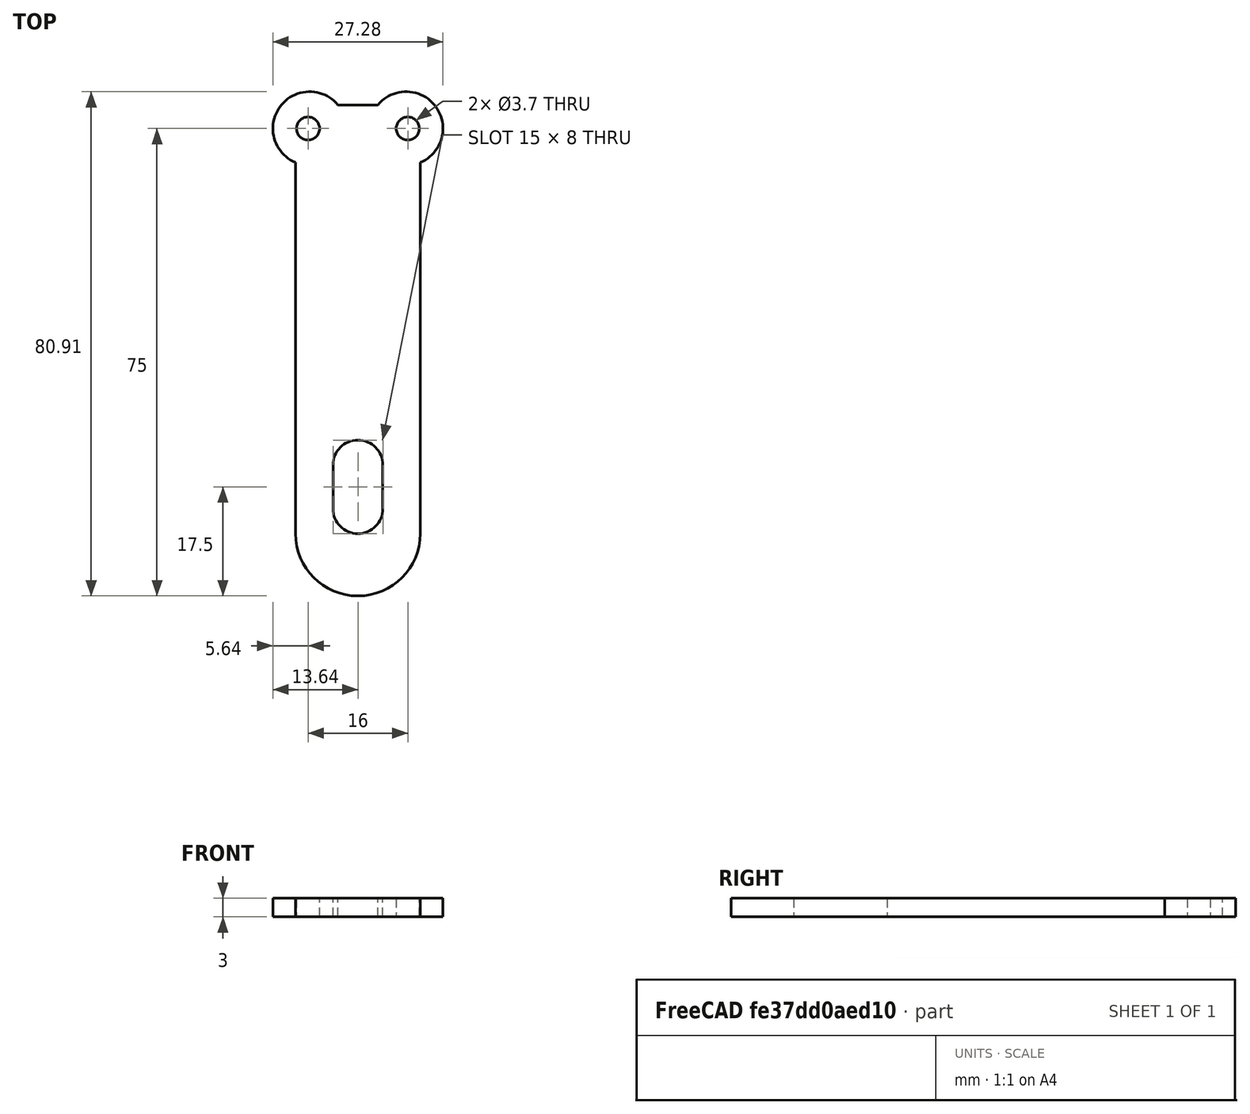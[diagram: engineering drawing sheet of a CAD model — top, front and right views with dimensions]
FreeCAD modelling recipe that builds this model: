
FCSTD DOCUMENT  (FreeCAD 0.19R24291 (Git))
Label: VX8PrintedCaseBeltClip
License: All rights reserved
LicenseURL: http://en.wikipedia.org/wiki/All_rights_reserved
objects: Sketcher::SketchObject×1, PartDesign::Pad×1, PartDesign::CoordinateSystem×1, PartDesign::Body×1
note: 5 computed .brp shape members not serialized (recipe doc carries the construction recipe); baked Part::Feature solids carry a one-line shape summary decoded from their .brp

FEATURE [Sketcher::SketchObject] Sketch
  FullyConstrained = false
  MapMode = 5
  Support = -> [XY_Plane]
  sketch-geometry (12):
    g0: ArcOfCircle CenterX=0 CenterY=0 CenterZ=0 NormalX=0 NormalY=0 NormalZ=1 AngleXU=0 Radius=10 StartAngle=3.14159 EndAngle=6.28319
    g1: LineSegment StartX=10 StartY=-2.4e-15 StartZ=0 EndX=10 EndY=59.5473 EndZ=0
    g2: LineSegment StartX=-10 StartY=59.5473 StartZ=0 EndX=-10 EndY=0 EndZ=0
    g3: ArcOfCircle CenterX=7.73152 CenterY=65 CenterZ=0 NormalX=0 NormalY=0 NormalZ=1 AngleXU=0 Radius=5.90571 StartAngle=5.10664 EndAngle=8.73046
    g4: ArcOfCircle CenterX=-7.73152 CenterY=65 CenterZ=0 NormalX=0 NormalY=0 NormalZ=1 AngleXU=0 Radius=5.90571 StartAngle=0.694322 EndAngle=4.31814
    g5: LineSegment StartX=-3.19305 StartY=68.7789 StartZ=0 EndX=3.19305 EndY=68.7789 EndZ=0
    g6: Circle CenterX=8 CenterY=65 CenterZ=0 NormalX=0 NormalY=0 NormalZ=1 AngleXU=0 Radius=1.85
    g7: Circle CenterX=-8 CenterY=65 CenterZ=0 NormalX=0 NormalY=0 NormalZ=1 AngleXU=0 Radius=1.85
    g8: ArcOfCircle CenterX=0 CenterY=11 CenterZ=0 NormalX=0 NormalY=0 NormalZ=1 AngleXU=0 Radius=4 StartAngle=0 EndAngle=3.14159
    g9: ArcOfCircle CenterX=0 CenterY=4 CenterZ=0 NormalX=0 NormalY=0 NormalZ=1 AngleXU=0 Radius=4 StartAngle=3.14159 EndAngle=6.28319
    g10: LineSegment StartX=-4 StartY=11 StartZ=0 EndX=-4 EndY=4 EndZ=0
    g11: LineSegment StartX=4 StartY=4 StartZ=0 EndX=4 EndY=11 EndZ=0
  constraints (34):
    c: Coincident(g0,g-1)
    c: PointOnObject(g0,g-1)
    c: PointOnObject(g0,g-1)
    c: Tangent(g0,g1) = -1.5708
    c: Coincident(g2,g0)
    c: Vertical(g2)
    c: Coincident(g3,g1)
    c: Coincident(g4,g2)
    c: Coincident(g5,g4)
    c: Coincident(g5,g3)
    c: Horizontal(g5)
    c: Symmetric(g4,g3,g-2)
    c: DistanceX(g0,g0) = 20
    c: DistanceY(g0,g3) = 65
    c: Horizontal(g2,g1)
    c: DistanceX(g7,g6) = 16
    c: Diameter(g6) = 3.7
    c: Equal(g7,g6)
    c: Symmetric(g7,g6,g-2)
    c: Horizontal(g3,g6)
    c: PointOnObject(g8,g-2)
    c: PointOnObject(g9,g-2)
    c: Coincident(g10,g8)
    c: Coincident(g10,g9)
    c: Vertical(g10)
    c: Coincident(g11,g9)
    c: Coincident(g11,g8)
    c: Horizontal(g8,g8)
    c: Horizontal(g8,g8)
    c: Horizontal(g9,g9)
    c: Horizontal(g9,g9)
    c: DistanceX(g8,g8) = 8
    c: DistanceY(g9,g8) = 7
    c: DistanceY(g8,g6) = 54
FEATURE [PartDesign::Pad] Pad
  Direction = (1,1,1)
  Length = 3
  Length2 = 100
  Profile = -> Sketch
  Type = 0
FEATURE [PartDesign::CoordinateSystem] Local_CS  label="MountScrew"
  AttacherType = Attacher::AttachEngine3D
  MapMode = 11
  Placement = pos=(-8,65,3) rot=(0,0,1;1.5708rad)
  Support = -> [Pad]
FEATURE [PartDesign::Body] Body  label="BeltClip"
  Group = -> [Sketch,Pad,Local_CS]
  Origin = -> Origin
  Tip = -> Pad
